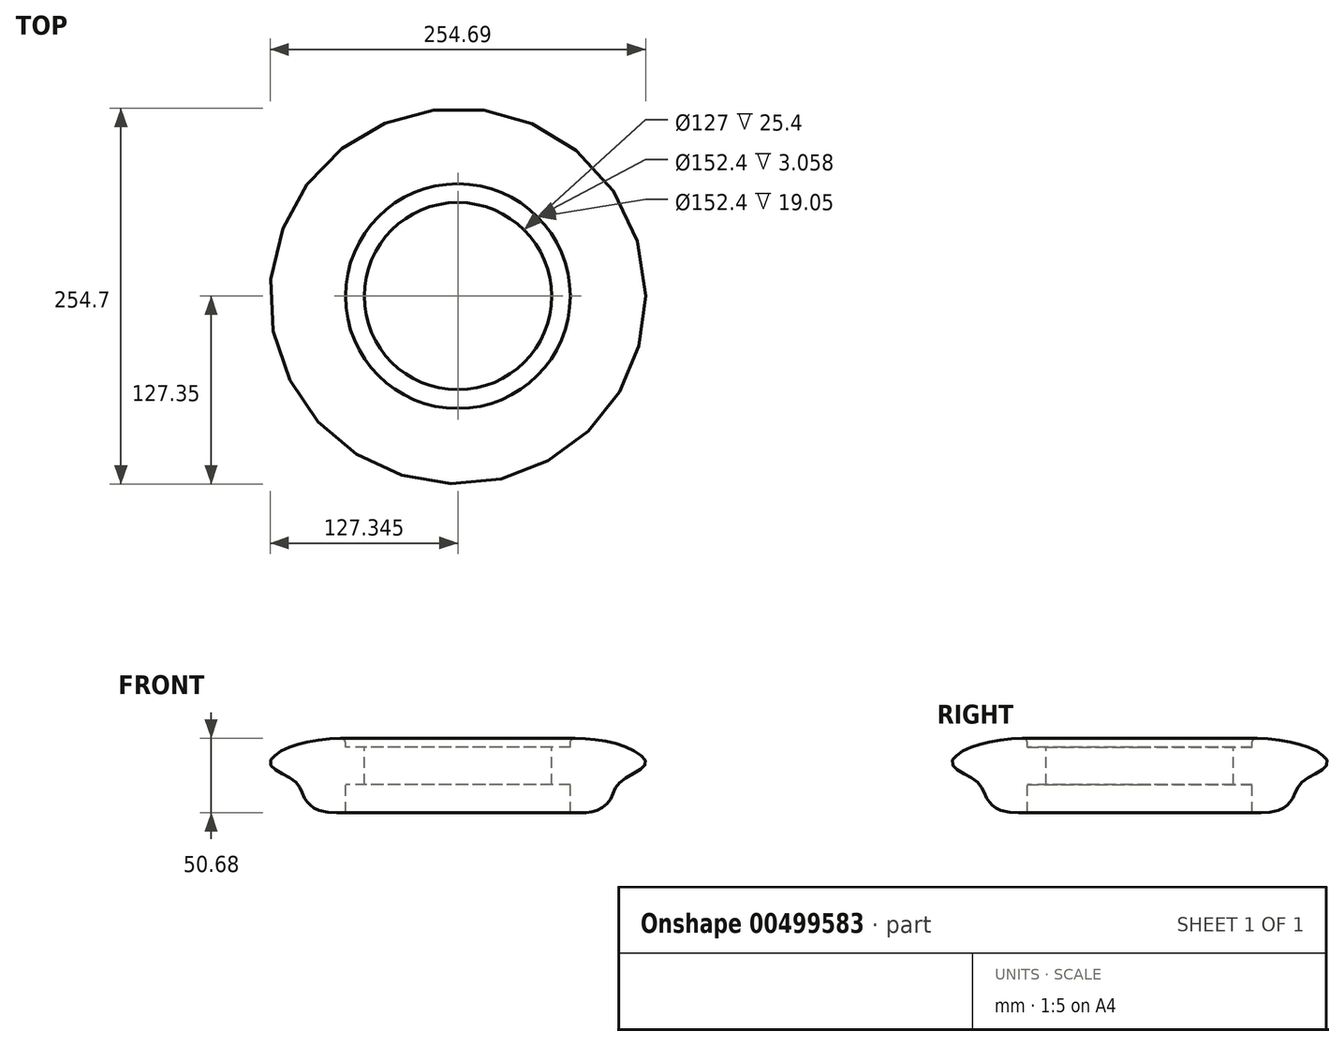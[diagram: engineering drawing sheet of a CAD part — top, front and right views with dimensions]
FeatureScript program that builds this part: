
annotation { "Feature Type Name" : "Feature", "Feature Type Description" : "" }
export const myFeature = defineFeature(function(context is Context, id is Id, definition is map)
    precondition{}
    {
        {
            var Q0;
            Q0=qCreatedBy(makeId("Front.planeOp"),FACE);
            var sketch = newSketch(context, id + "F0", { "sketchPlane" : qUnion([Q0])});
            skLineSegment(sketch, "E0", {"start": v(13.04, -11.08) * mm, "end": v(13.04, 14.32) * mm});
            skLineSegment(sketch, "E1", {"start": v(13.04, -11.08) * mm, "end": v(0.34, -11.08) * mm});
            skLineSegment(sketch, "E2", {"start": v(13.04, 14.32) * mm, "end": v(0.34, 14.32) * mm});
            skLineSegment(sketch, "E3", {"start": v(0.34, -11.08) * mm, "end": v(0.34, -30.13) * mm});
            skLineSegment(sketch, "E4", {"start": v(0.34, 14.32) * mm, "end": v(0.34, 20.67) * mm});
            skFitSpline(sketch, "E5", {"points": [v(0.34, -30.13) * mm, v(-16.71, -28.72) * mm, v(-26.59, -21.39) * mm, v(-33.63, -9.06) * mm, v(-50.68, 3.07) * mm, v(-36.75, 14.87) * mm, v(0.34, 20.67) * mm], "startDerivative": vector(-163.52, 1.27) * mm, "endDerivative": vector(153.64, 4.81) * mm});
            skLineSegment(sketch, "E6", {"start": v(76.54, 31.38) * mm, "end": v(76.54, -33.23) * mm, "construction": true});
            skSolve(sketch);
        }
        {
            var Q0;
            Q0=makeQuery(id+"F0.imprint","IMPRINT",FACE,{"disambiguationData":[TD([[makeQuery(id+"F0.imprint","IMPRINT",EDGE,{"derivedFrom":sQuery(id+"F0.wireOp",EDGE,"E0")}),1.0]])]});
            var Q1;
            Q1=sQuery(id+"F0.wireOp",EDGE,"E6");
            revolve(context, id + "F1", {"entities" : qUnion([Q0]), "axis" : qUnion([Q1]), "revolveType" : RevolveType.FULL});
        }
        {
            var Q0;
            Q0=makeQuery(id+"F1.opRevolve","SWEPT_EDGE",EDGE,{"disambiguationData":[OSD([sQuery(id+"F0.wireOp",EDGE,"E4"),sQuery(id+"F0.wireOp",EDGE,"E5")])]});
            fillet(context, id + "F2", {"entities" : qUnion([Q0]), "radius" : 3.17 * mm, "tangentPropagation" : true, "allowEdgeOverflow" : false});
        }
    });
